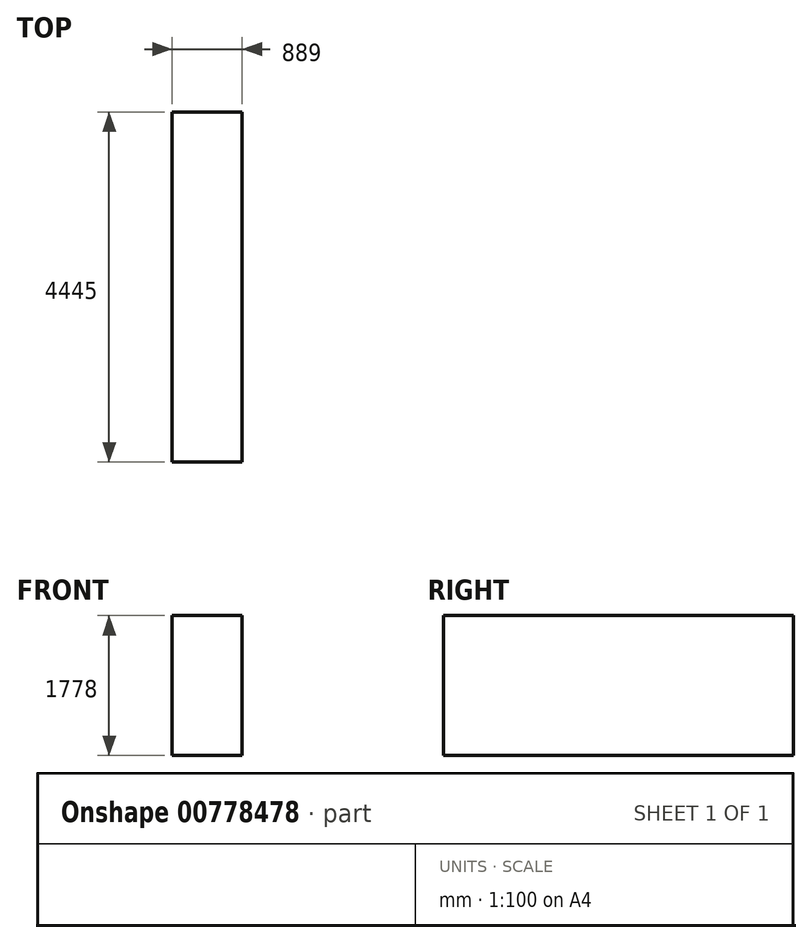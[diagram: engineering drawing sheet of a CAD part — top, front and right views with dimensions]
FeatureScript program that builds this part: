
annotation { "Feature Type Name" : "Feature", "Feature Type Description" : "" }
export const myFeature = defineFeature(function(context is Context, id is Id, definition is map)
    precondition{}
    {
        {
            var Q0;
            Q0=qCreatedBy(makeId("Top.planeOp"),FACE);
            var sketch = newSketch(context, id + "F0", { "sketchPlane" : qUnion([Q0])});
            skLineSegment(sketch, "E0.bottom", {"start": v(0, 0) * mm, "end": v(889, 0) * mm});
            skLineSegment(sketch, "E0.top", {"start": v(0, -4445) * mm, "end": v(889, -4445) * mm});
            skLineSegment(sketch, "E0.left", {"start": v(0, 0) * mm, "end": v(0, -4445) * mm});
            skLineSegment(sketch, "E0.right", {"start": v(889, 0) * mm, "end": v(889, -4445) * mm});
            skSolve(sketch);
        }
        {
            var Q0;
            Q0=makeQuery(id+"F0.imprint","IMPRINT",FACE,{"disambiguationData":[TD([[makeQuery(id+"F0.imprint","IMPRINT",EDGE,{"derivedFrom":sQuery(id+"F0.wireOp",EDGE,"E0.bottom")}),-1.0]])]});
            extrude(context, id + "F1", {"entities" : qUnion([Q0]), "depth" : 1778 * mm, "offsetDistance" : 25.4 * mm});
        }
    });
